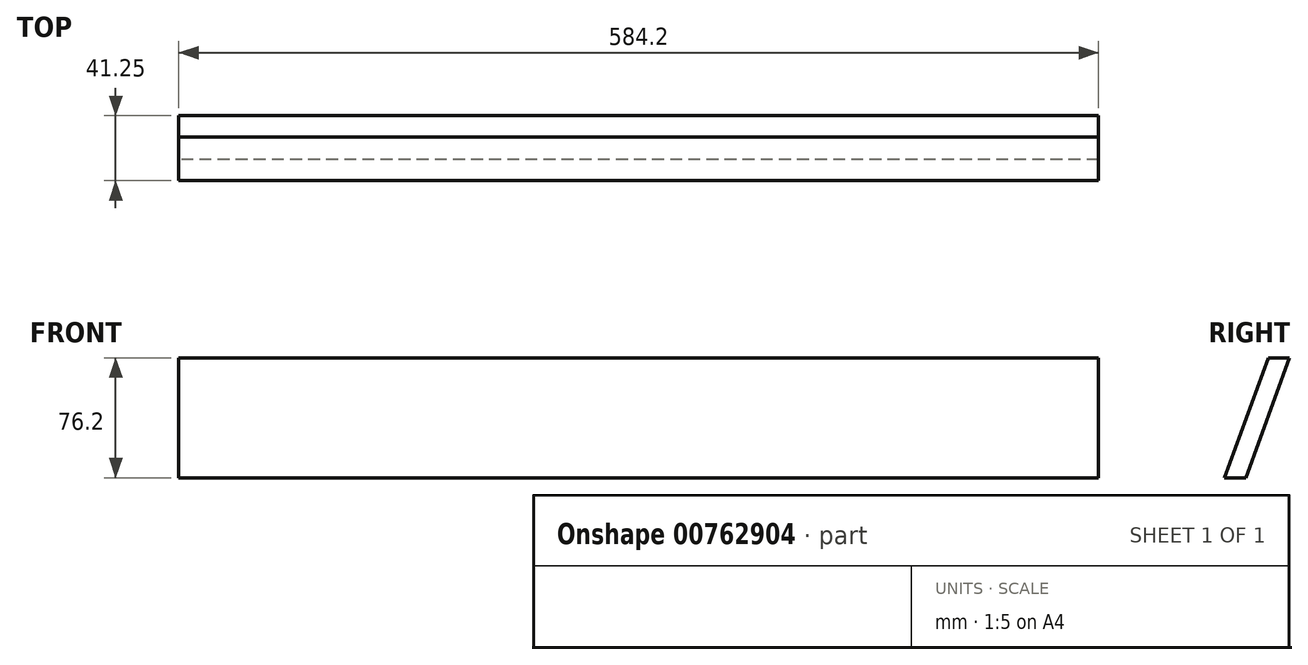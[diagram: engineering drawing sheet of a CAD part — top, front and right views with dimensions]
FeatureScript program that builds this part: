
annotation { "Feature Type Name" : "Feature", "Feature Type Description" : "" }
export const myFeature = defineFeature(function(context is Context, id is Id, definition is map)
    precondition{}
    {
        {
            var Q0;
            Q0=qCreatedBy(makeId("Right.planeOp"),FACE);
            var sketch = newSketch(context, id + "F0", { "sketchPlane" : qUnion([Q0])});
            skLineSegment(sketch, "E0", {"start": v(-27.74, 76.2) * mm, "end": v(-41.25, 76.2) * mm, "construction": true});
            skLineSegment(sketch, "E1", {"start": v(-41.25, 76.2) * mm, "end": v(-13.52, 0) * mm, "construction": true});
            skLineSegment(sketch, "E2", {"start": v(-13.52, 0) * mm, "end": v(0, 0) * mm, "construction": true});
            skLineSegment(sketch, "E3", {"start": v(0, 0) * mm, "end": v(-27.74, 76.2) * mm, "construction": true});
            skLineSegment(sketch, "E4", {"start": v(0, 0) * mm, "end": v(0, 78.25) * mm, "construction": true});
            skLineSegment(sketch, "E5.MirrorCS", {"start": v(0, 0) * mm, "end": v(27.74, 76.2) * mm});
            skLineSegment(sketch, "E6.MirrorCS", {"start": v(13.52, 0) * mm, "end": v(0, 0) * mm});
            skLineSegment(sketch, "E7.MirrorCS", {"start": v(27.74, 76.2) * mm, "end": v(41.25, 76.2) * mm});
            skLineSegment(sketch, "E8.MirrorCS", {"start": v(41.25, 76.2) * mm, "end": v(13.52, 0) * mm});
            skSolve(sketch);
        }
        {
            var Q0;
            Q0 = qSketchRegion(id + "F0", true);
            extrude(context, id + "F1", {"entities" : qUnion([Q0]), "depth" : 584.2 * mm, "offsetDistance" : 25.4 * mm, "symmetric" : true});
        }
    });
